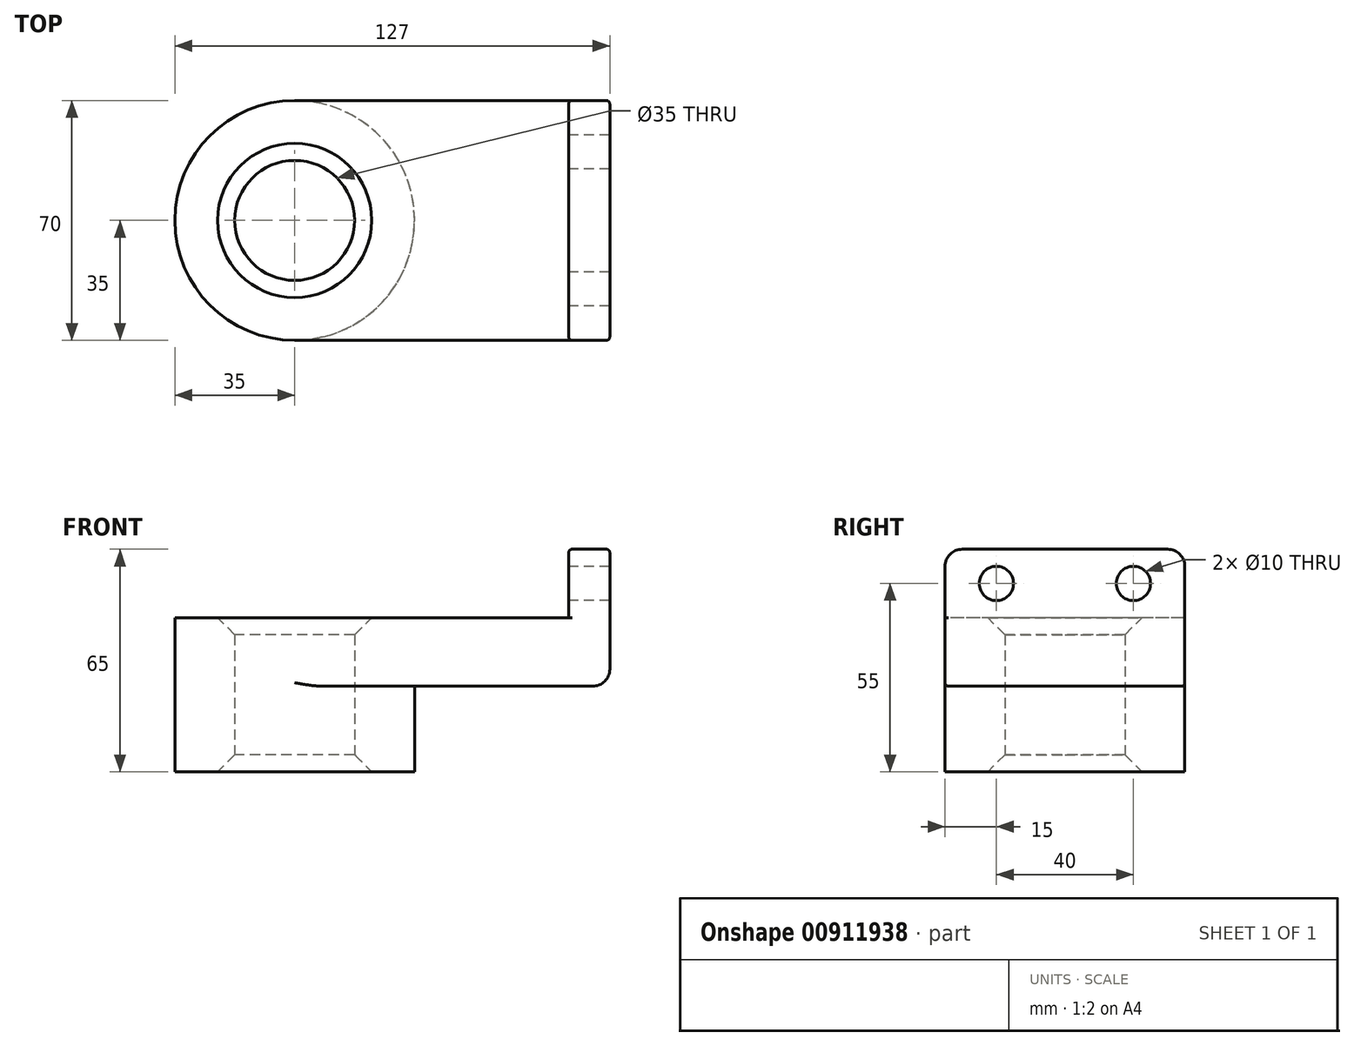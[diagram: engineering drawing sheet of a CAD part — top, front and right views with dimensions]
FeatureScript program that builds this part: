
annotation { "Feature Type Name" : "Feature", "Feature Type Description" : "" }
export const myFeature = defineFeature(function(context is Context, id is Id, definition is map)
    precondition{}
    {
        {
            var Q0;
            Q0=qCreatedBy(makeId("Top.planeOp"),FACE);
            var sketch = newSketch(context, id + "F0", { "sketchPlane" : qUnion([Q0])});
            skLineSegment(sketch, "E0.rect.bottom", {"start": v(40, 35) * mm, "end": v(-40, 35) * mm});
            skLineSegment(sketch, "E0.rect.top", {"start": v(40, -35) * mm, "end": v(-40, -35) * mm});
            skLineSegment(sketch, "E0.rect.left", {"start": v(40, 35) * mm, "end": v(40, -35) * mm});
            skLineSegment(sketch, "E0.rect.right", {"start": v(-40, 35) * mm, "end": v(-40, -35) * mm});
            skPoint(sketch, "E0.rect.middle", {"position": v(0, 0) * mm});
            skCircle(sketch, "E1", {"center": v(-40, 0) * mm, "radius": 35 * mm});
            skCircle(sketch, "E2", {"center": v(-40, 0) * mm, "radius": 17.5 * mm});
            skSolve(sketch);
        }
        {
            var Q0;
            {var subQ1=sQuery(id+"F0.wireOp",EDGE,"E0.rect.right");var subQ3=sQuery(id+"F0.wireOp",EDGE,"E2");var subQ4=makeQuery(id+"F0.imprint","INTERSECT",VERTEX,{"disambiguationData":[OD(0.0)],"derivedFrom":[subQ1,subQ3]});Q0=makeQuery(id+"F0.imprint","IMPRINT",FACE,{"disambiguationData":[TD([[makeQuery(id+"F0.imprint","IMPRINT",EDGE,{"disambiguationData":[TD([[subQ4,-1.0]])],"derivedFrom":subQ3}),-1.0]])]});}
            var Q1;
            {var subQ1=sQuery(id+"F0.wireOp",EDGE,"E0.rect.right");var subQ3=sQuery(id+"F0.wireOp",EDGE,"E2");var subQ4=makeQuery(id+"F0.imprint","INTERSECT",VERTEX,{"disambiguationData":[OD(0.0)],"derivedFrom":[subQ1,subQ3]});Q1=makeQuery(id+"F0.imprint","IMPRINT",FACE,{"disambiguationData":[TD([[makeQuery(id+"F0.imprint","IMPRINT",EDGE,{"disambiguationData":[TD([[subQ4,1.0]])],"derivedFrom":subQ3}),-1.0]])]});}
            var Q2;
            {var subQ0=sQuery(id+"F0.wireOp",EDGE,"E0.rect.bottom");Q2=makeQuery(id+"F0.imprint","IMPRINT",FACE,{"disambiguationData":[TD([[makeQuery(id+"F0.imprint","IMPRINT",EDGE,{"derivedFrom":subQ0}),1.0]])]});}
            extrude(context, id + "F1", {"entities" : qUnion([Q0, Q1, Q2]), "offsetDistance" : 25 * mm, "depth" : 20 * mm});
        }
        {
            var Q0;
            {var subQ1=sQuery(id+"F0.wireOp",EDGE,"E0.rect.right");var subQ3=sQuery(id+"F0.wireOp",EDGE,"E2");var subQ4=makeQuery(id+"F0.imprint","INTERSECT",VERTEX,{"disambiguationData":[OD(0.0)],"derivedFrom":[subQ1,subQ3]});Q0=makeQuery(id+"F0.imprint","IMPRINT",FACE,{"disambiguationData":[TD([[makeQuery(id+"F0.imprint","IMPRINT",EDGE,{"disambiguationData":[TD([[subQ4,1.0]])],"derivedFrom":subQ3}),-1.0]])]});}
            var Q1;
            {var subQ1=sQuery(id+"F0.wireOp",EDGE,"E0.rect.right");var subQ3=sQuery(id+"F0.wireOp",EDGE,"E2");var subQ4=makeQuery(id+"F0.imprint","INTERSECT",VERTEX,{"disambiguationData":[OD(0.0)],"derivedFrom":[subQ1,subQ3]});Q1=makeQuery(id+"F0.imprint","IMPRINT",FACE,{"disambiguationData":[TD([[makeQuery(id+"F0.imprint","IMPRINT",EDGE,{"disambiguationData":[TD([[subQ4,-1.0]])],"derivedFrom":subQ3}),-1.0]])]});}
            extrude(context, id + "F2", {"entities" : qUnion([Q0, Q1]), "operationType" : NewBodyOperationType.ADD, "oppositeDirection" : true, "offsetDistance" : 25 * mm, "depth" : 25 * mm});
        }
        {
            var Q0;
            Q0=makeQuery(id+"F1.opExtrude","SWEPT_FACE",FACE,{"disambiguationData":[OSD([sQuery(id+"F0.wireOp",EDGE,"E0.rect.left")])]});
            var sketch = newSketch(context, id + "F3", { "sketchPlane" : qUnion([Q0])});
            skLineSegment(sketch, "E3.bottom", {"start": v(35, 0) * mm, "end": v(-35, 0) * mm});
            skLineSegment(sketch, "E3.top", {"start": v(35, 40) * mm, "end": v(-35, 40) * mm});
            skLineSegment(sketch, "E3.left", {"start": v(35, 0) * mm, "end": v(35, 40) * mm});
            skLineSegment(sketch, "E3.right", {"start": v(-35, 0) * mm, "end": v(-35, 40) * mm});
            skCircle(sketch, "E4", {"center": v(20, 30) * mm, "radius": 5 * mm});
            skLineSegment(sketch, "E5", {"start": v(0, 40) * mm, "end": v(0, -32.88) * mm, "construction": true});
            skPoint(sketch, "E5.endSnap0", {"position": v(0, 20) * mm});
            skCircle(sketch, "E6.MirrorC", {"center": v(-20, 30) * mm, "radius": 5 * mm});
            skSolve(sketch);
        }
        {
            var Q0;
            {var subQ0=sQuery(id+"F3.wireOp",EDGE,"E3.bottom");Q0=makeQuery(id+"F3.imprint","IMPRINT",FACE,{"disambiguationData":[TD([[makeQuery(id+"F3.imprint","IMPRINT",EDGE,{"derivedFrom":subQ0}),-1.0]])]});}
            var Q1;
            {var subQ2=sQuery(id+"F3.wireOp",EDGE,"E3.top");Q1=makeQuery(id+"F3.imprint","IMPRINT",FACE,{"disambiguationData":[TD([[makeQuery(id+"F3.imprint","IMPRINT",EDGE,{"derivedFrom":subQ2}),1.0]])]});}
            extrude(context, id + "F4", {"entities" : qUnion([Q0, Q1]), "operationType" : NewBodyOperationType.ADD, "offsetDistance" : 25 * mm, "depth" : 12 * mm});
        }
        {
            var Q0;
            Q0=makeQuery(id+"F2.opExtrude","CAP_EDGE",EDGE,{"disambiguationData":[OSD([sQuery(id+"F0.wireOp",EDGE,"E1")])],"isStart":true});
            var Q1;
            Q1=makeQuery(id+"F4.opExtrude","CAP_EDGE",EDGE,{"disambiguationData":[OSD([sQuery(id+"F3.wireOp",EDGE,"E3.bottom")])],"isStart":false});
            var Q2;
            Q2=makeQuery(id+"F4.opExtrude","SWEPT_EDGE",EDGE,{"disambiguationData":[OSD([sQuery(id+"F3.wireOp",EDGE,"E3.top"),sQuery(id+"F3.wireOp",EDGE,"E3.left")])]});
            var Q3;
            Q3=makeQuery(id+"F4.opExtrude","SWEPT_EDGE",EDGE,{"disambiguationData":[OSD([sQuery(id+"F3.wireOp",EDGE,"E3.top"),sQuery(id+"F3.wireOp",EDGE,"E3.right")])]});
            fillet(context, id + "F5", {"entities" : qUnion([Q0, Q1, Q2, Q3]), "radius" : 5 * mm, "tangentPropagation" : true, "allowEdgeOverflow" : false});
        }
        {
            var Q0;
            {var subQ0=sQuery(id+"F0.wireOp",EDGE,"E2");Q0=makeQuery(id+"F2.boolean.opBoolean","MERGE",FACE,{"derivedFrom":[makeQuery(id+"F1.opExtrude","SWEPT_FACE",FACE,{"disambiguationData":[OSD([subQ0])]}),makeQuery(id+"F2.opExtrude","SWEPT_FACE",FACE,{"disambiguationData":[OSD([subQ0])]})]});}
            chamfer(context, id + "F6", {"entities" : qUnion([Q0]), "width" : 5 * mm, "tangentPropagation" : true});
        }
        {
            var Q0;
            Q0=makeQuery(id+"F4.opExtrude","CAP_EDGE",EDGE,{"disambiguationData":[OSD([sQuery(id+"F3.wireOp",EDGE,"E3.top")])],"isStart":true});
            var Q1;
            Q1=makeQuery(id+"F4.opExtrude","CAP_EDGE",EDGE,{"disambiguationData":[OSD([sQuery(id+"F3.wireOp",EDGE,"E3.top")])],"isStart":false});
            var Q2;
            Q2=makeQuery(id+"F1.opExtrude","CAP_EDGE",EDGE,{"disambiguationData":[OSD([sQuery(id+"F0.wireOp",EDGE,"E0.rect.left")])],"isStart":false});
            fillet(context, id + "F7", {"entities" : qUnion([Q0, Q1, Q2]), "radius" : 1 * mm, "tangentPropagation" : true, "allowEdgeOverflow" : false});
        }
    });
